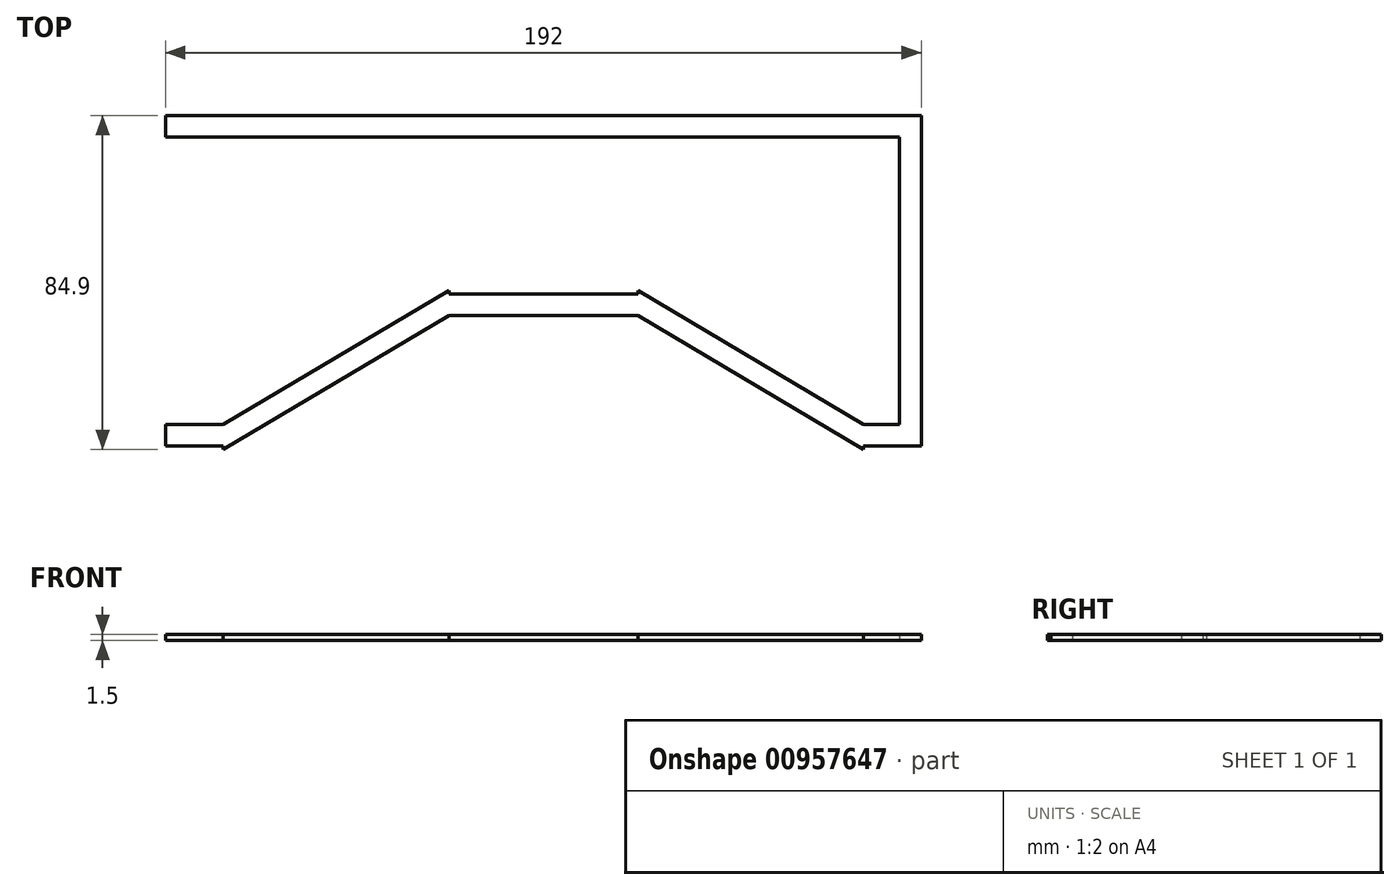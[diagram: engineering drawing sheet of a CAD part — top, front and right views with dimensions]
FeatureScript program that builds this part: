
annotation { "Feature Type Name" : "Feature", "Feature Type Description" : "" }
export const myFeature = defineFeature(function(context is Context, id is Id, definition is map)
    precondition{}
    {
        {
            var Q0;
            Q0=qCreatedBy(makeId("Top.planeOp"),FACE);
            var sketch = newSketch(context, id + "F0", { "sketchPlane" : qUnion([Q0])});
            skLineSegment(sketch, "E0.bottom", {"start": v(-96, 57.45) * mm, "end": v(0, 57.45) * mm});
            skLineSegment(sketch, "E0.top", {"start": v(-96, 51.95) * mm, "end": v(0, 51.95) * mm});
            skLineSegment(sketch, "E0.left", {"start": v(-96, 57.45) * mm, "end": v(-96, 51.95) * mm});
            skLineSegment(sketch, "E0.right", {"start": v(0, 57.45) * mm, "end": v(0, 51.95) * mm});
            skLineSegment(sketch, "E1.MirrorCS", {"start": v(96, 57.45) * mm, "end": v(0, 57.45) * mm});
            skLineSegment(sketch, "E2.MirrorCS", {"start": v(96, 51.95) * mm, "end": v(0, 51.95) * mm});
            skLineSegment(sketch, "E3.MirrorCS", {"start": v(96, 57.45) * mm, "end": v(96, 51.95) * mm});
            skLineSegment(sketch, "E4.bottom", {"start": v(-96, 51.95) * mm, "end": v(-90.5, 51.95) * mm});
            skLineSegment(sketch, "E4.top", {"start": v(-96, -21.05) * mm, "end": v(-90.5, -21.05) * mm});
            skLineSegment(sketch, "E4.left", {"start": v(-96, 51.95) * mm, "end": v(-96, -21.05) * mm});
            skLineSegment(sketch, "E4.right", {"start": v(-90.5, 51.95) * mm, "end": v(-90.5, -21.05) * mm});
            skLineSegment(sketch, "E5.bottom", {"start": v(-96, -21.05) * mm, "end": v(-81.33, -21.05) * mm});
            skLineSegment(sketch, "E5.top", {"start": v(-96, -26.55) * mm, "end": v(-81.33, -26.55) * mm});
            skLineSegment(sketch, "E5.left", {"start": v(-96, -21.05) * mm, "end": v(-96, -26.55) * mm});
            skLineSegment(sketch, "E5.right", {"start": v(-81.33, -21.05) * mm, "end": v(-81.33, -26.55) * mm});
            skLineSegment(sketch, "E6.MirrorCS", {"start": v(90.5, 51.95) * mm, "end": v(90.5, -21.05) * mm});
            skLineSegment(sketch, "E7.MirrorCS", {"start": v(96, 51.95) * mm, "end": v(96, -21.05) * mm});
            skLineSegment(sketch, "E8.MirrorCS", {"start": v(96, -21.05) * mm, "end": v(81.33, -21.05) * mm});
            skLineSegment(sketch, "E9.MirrorCS", {"start": v(96, -26.55) * mm, "end": v(81.33, -26.55) * mm});
            skLineSegment(sketch, "E10.MirrorCS", {"start": v(81.33, -21.05) * mm, "end": v(81.33, -26.55) * mm});
            skLineSegment(sketch, "E11.MirrorCS", {"start": v(96, -21.05) * mm, "end": v(96, -26.55) * mm});
            skLineSegment(sketch, "E12.bottom", {"start": v(-24, 12.07) * mm, "end": v(24, 12.07) * mm});
            skLineSegment(sketch, "E12.top", {"start": v(-24, 6.57) * mm, "end": v(24, 6.57) * mm});
            skLineSegment(sketch, "E12.left", {"start": v(-24, 12.07) * mm, "end": v(-24, 6.57) * mm});
            skLineSegment(sketch, "E12.right", {"start": v(24, 12.07) * mm, "end": v(24, 6.57) * mm});
            skLineSegment(sketch, "E13", {"start": v(-81.33, -21.05) * mm, "end": v(-24, 12.97) * mm});
            skLineSegment(sketch, "E14", {"start": v(-81.33, -27.45) * mm, "end": v(-24, 6.57) * mm});
            skLineSegment(sketch, "E15.MirrorCS", {"start": v(81.33, -21.05) * mm, "end": v(24, 12.97) * mm});
            skLineSegment(sketch, "E16.MirrorCS", {"start": v(81.33, -27.45) * mm, "end": v(24, 6.57) * mm});
            skLineSegment(sketch, "E17", {"start": v(-81.32, -27.45) * mm, "end": v(-81.32, -26.55) * mm});
            skLineSegment(sketch, "E18", {"start": v(-24, 12.97) * mm, "end": v(-24, 12.07) * mm});
            skLineSegment(sketch, "E19", {"start": v(24, 12.97) * mm, "end": v(24, 12.07) * mm});
            skLineSegment(sketch, "E20", {"start": v(81.33, -27.45) * mm, "end": v(81.33, -26.55) * mm});
            skSolve(sketch);
        }
        {
            var Q0;
            Q0=makeQuery(id+"F0.imprint","IMPRINT",FACE,{"disambiguationData":[TD([[makeQuery(id+"F0.imprint","IMPRINT",EDGE,{"derivedFrom":sQuery(id+"F0.wireOp",EDGE,"E4.bottom")}),-1.0]])]});
            var Q1;
            Q1=makeQuery(id+"F0.imprint","IMPRINT",FACE,{"disambiguationData":[TD([[makeQuery(id+"F0.imprint","IMPRINT",EDGE,{"derivedFrom":sQuery(id+"F0.wireOp",EDGE,"E0.bottom")}),-1.0]])]});
            var Q2;
            {var subQ1=sQuery(id+"F0.wireOp",EDGE,"E0.right");Q2=makeQuery(id+"F0.imprint","IMPRINT",FACE,{"disambiguationData":[TD([[makeQuery(id+"F0.imprint","IMPRINT",EDGE,{"derivedFrom":subQ1}),1.0]])]});}
            var Q3;
            {var subQ2=sQuery(id+"F0.wireOp",EDGE,"E6.MirrorCS");Q3=makeQuery(id+"F0.imprint","IMPRINT",FACE,{"disambiguationData":[TD([[makeQuery(id+"F0.imprint","IMPRINT",EDGE,{"derivedFrom":subQ2}),1.0]])]});}
            var Q4;
            Q4=makeQuery(id+"F0.imprint","IMPRINT",FACE,{"disambiguationData":[TD([[makeQuery(id+"F0.imprint","IMPRINT",EDGE,{"derivedFrom":sQuery(id+"F0.wireOp",EDGE,"E9.MirrorCS")}),-1.0]])]});
            var Q5;
            Q5=makeQuery(id+"F0.imprint","IMPRINT",FACE,{"disambiguationData":[TD([[makeQuery(id+"F0.imprint","IMPRINT",EDGE,{"derivedFrom":sQuery(id+"F0.wireOp",EDGE,"E10.MirrorCS")}),-1.0]])]});
            var Q6;
            Q6=makeQuery(id+"F0.imprint","IMPRINT",FACE,{"disambiguationData":[TD([[makeQuery(id+"F0.imprint","IMPRINT",EDGE,{"derivedFrom":sQuery(id+"F0.wireOp",EDGE,"E12.bottom")}),-1.0]])]});
            var Q7;
            Q7=makeQuery(id+"F0.imprint","IMPRINT",FACE,{"disambiguationData":[TD([[makeQuery(id+"F0.imprint","IMPRINT",EDGE,{"derivedFrom":sQuery(id+"F0.wireOp",EDGE,"E5.right")}),1.0]])]});
            var Q8;
            Q8=makeQuery(id+"F0.imprint","IMPRINT",FACE,{"disambiguationData":[TD([[makeQuery(id+"F0.imprint","IMPRINT",EDGE,{"derivedFrom":sQuery(id+"F0.wireOp",EDGE,"E5.top")}),1.0]])]});
            extrude(context, id + "F1", {"entities" : qUnion([Q0, Q1, Q2, Q3, Q4, Q5, Q6, Q7, Q8]), "depth" : 1.5 * mm, "offsetDistance" : 25 * mm});
        }
    });
